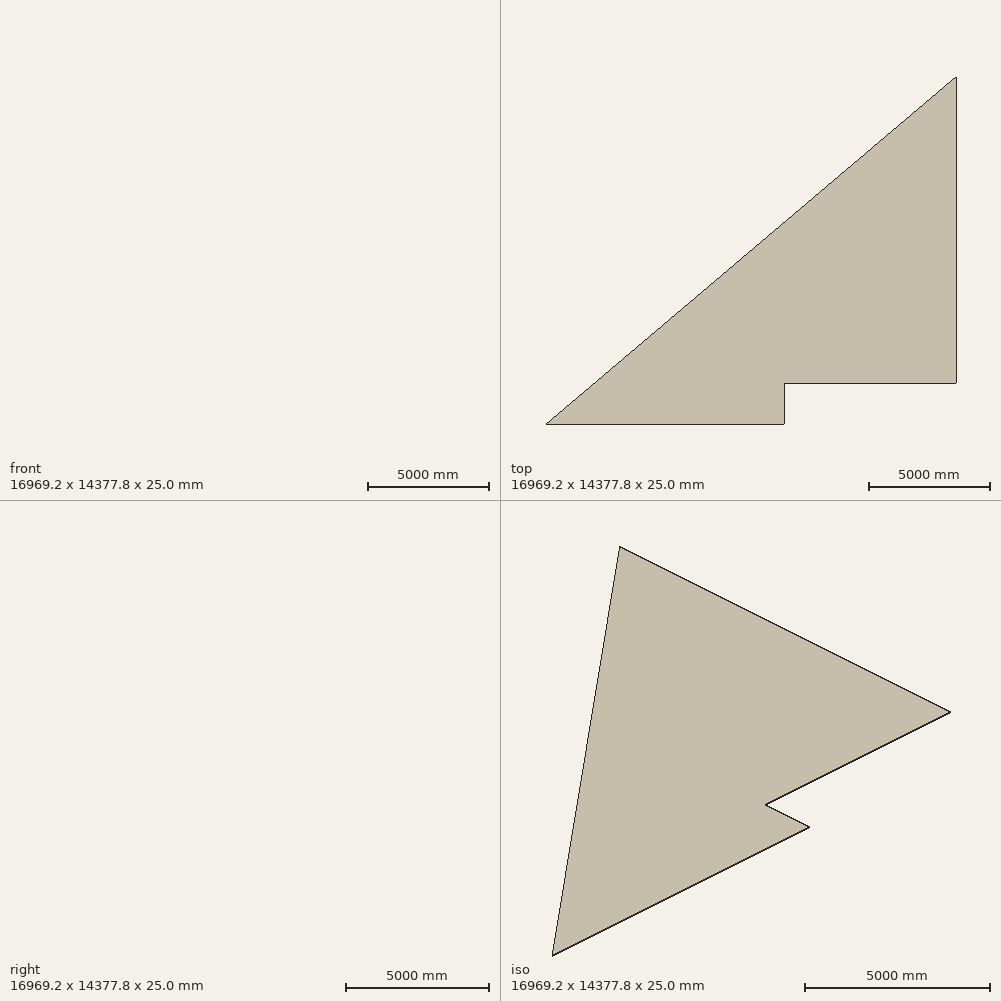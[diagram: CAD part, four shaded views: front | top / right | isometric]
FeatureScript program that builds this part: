
annotation { "Feature Type Name" : "Feature", "Feature Type Description" : "" }
export const myFeature = defineFeature(function(context is Context, id is Id, definition is map)
    precondition{}
    {
        {
            var Q0;
            Q0=qCreatedBy(makeId("Top.planeOp"),FACE);
            var sketch = newSketch(context, id + "F0", { "sketchPlane" : qUnion([Q0])});
            skLineSegment(sketch, "E0", {"start": v(0, 1700) * mm, "end": v(0, 13700) * mm, "construction": true});
            skLineSegment(sketch, "E1", {"start": v(0, 13700) * mm, "end": v(-16169.19, 0) * mm});
            skLineSegment(sketch, "E2", {"start": v(-16169.19, 0) * mm, "end": v(-10150, 0) * mm});
            skLineSegment(sketch, "E3", {"start": v(-6320, 0) * mm, "end": v(-6320, 1700) * mm});
            skLineSegment(sketch, "E4", {"start": v(-6320, 1700) * mm, "end": v(0, 1700) * mm});
            skLineSegment(sketch, "E5", {"start": v(0, 1700) * mm, "end": v(800, 1700) * mm});
            skLineSegment(sketch, "E6", {"start": v(800, 1700) * mm, "end": v(800, 14377.83) * mm});
            skLineSegment(sketch, "E7", {"start": v(800, 14377.83) * mm, "end": v(0, 13700) * mm});
            skLineSegment(sketch, "E8", {"start": v(-10150, 0) * mm, "end": v(-10150, 5100) * mm, "construction": true});
            skLineSegment(sketch, "E9", {"start": v(-10150, 0) * mm, "end": v(-6320, 0) * mm});
            skSolve(sketch);
        }
        {
            var Q0;
            Q0 = qSketchRegion(id + "F0", true);
            extrude(context, id + "F1", {"entities" : qUnion([Q0]), "oppositeDirection" : true, "depth" : 25 * mm, "offsetDistance" : 25 * mm});
        }
    });
